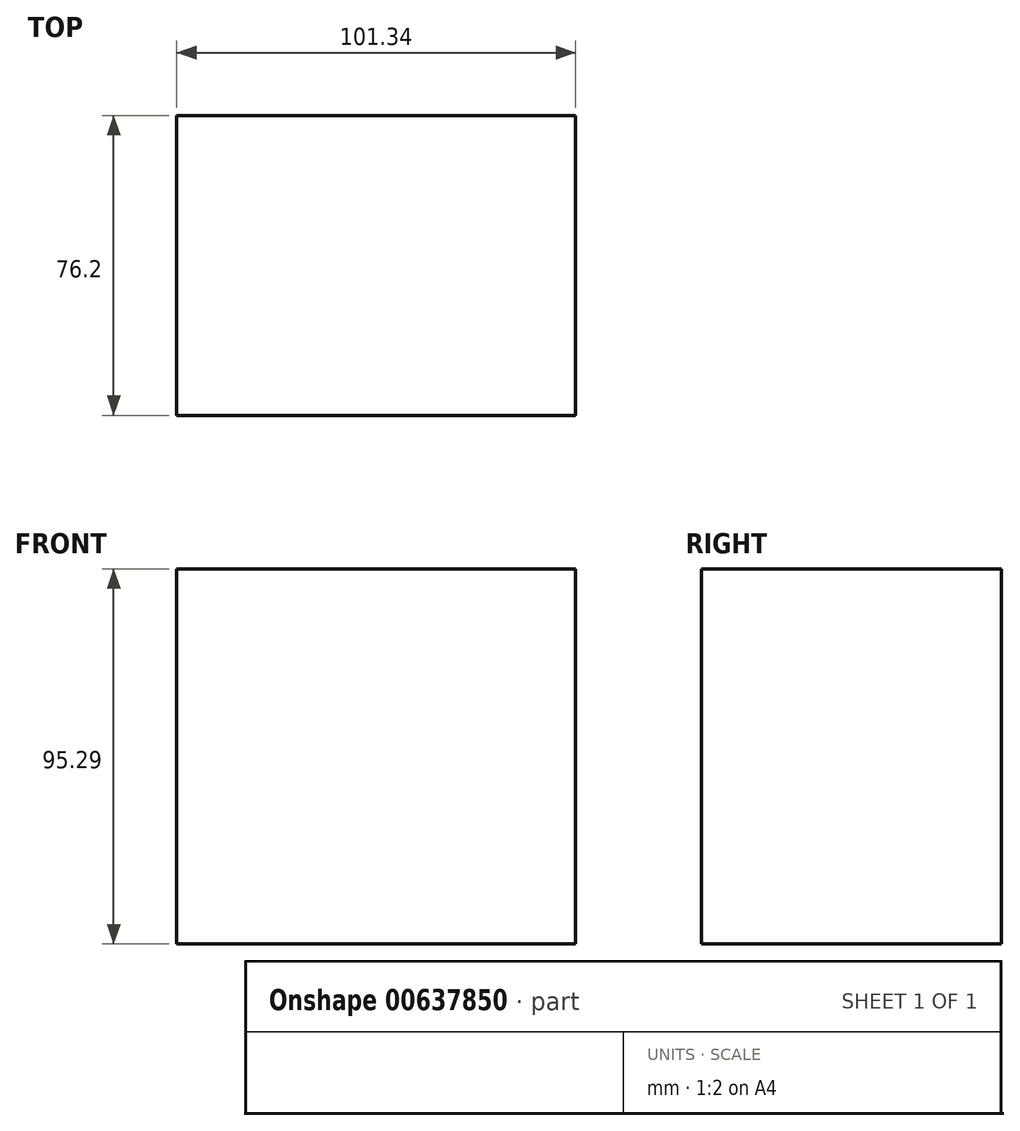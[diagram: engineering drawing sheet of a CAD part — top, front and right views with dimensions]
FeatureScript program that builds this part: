
annotation { "Feature Type Name" : "Feature", "Feature Type Description" : "" }
export const myFeature = defineFeature(function(context is Context, id is Id, definition is map)
    precondition{}
    {
        {
            var Q0;
            Q0=qCreatedBy(makeId("Front.planeOp"),FACE);
            var sketch = newSketch(context, id + "F0", { "sketchPlane" : qUnion([Q0])});
            skLineSegment(sketch, "E0.bottom", {"start": v(-50.52, 52.94) * mm, "end": v(50.82, 52.94) * mm});
            skLineSegment(sketch, "E0.top", {"start": v(-50.52, -42.35) * mm, "end": v(50.82, -42.35) * mm});
            skLineSegment(sketch, "E0.left", {"start": v(-50.52, 52.94) * mm, "end": v(-50.52, -42.35) * mm});
            skLineSegment(sketch, "E0.right", {"start": v(50.82, 52.94) * mm, "end": v(50.82, -42.35) * mm});
            skSolve(sketch);
        }
        {
            var Q0;
            Q0 = qSketchRegion(id + "F0", true);
            extrude(context, id + "F1", {"entities" : qUnion([Q0]), "depth" : 76.2 * mm, "offsetDistance" : 25.4 * mm});
        }
    });
